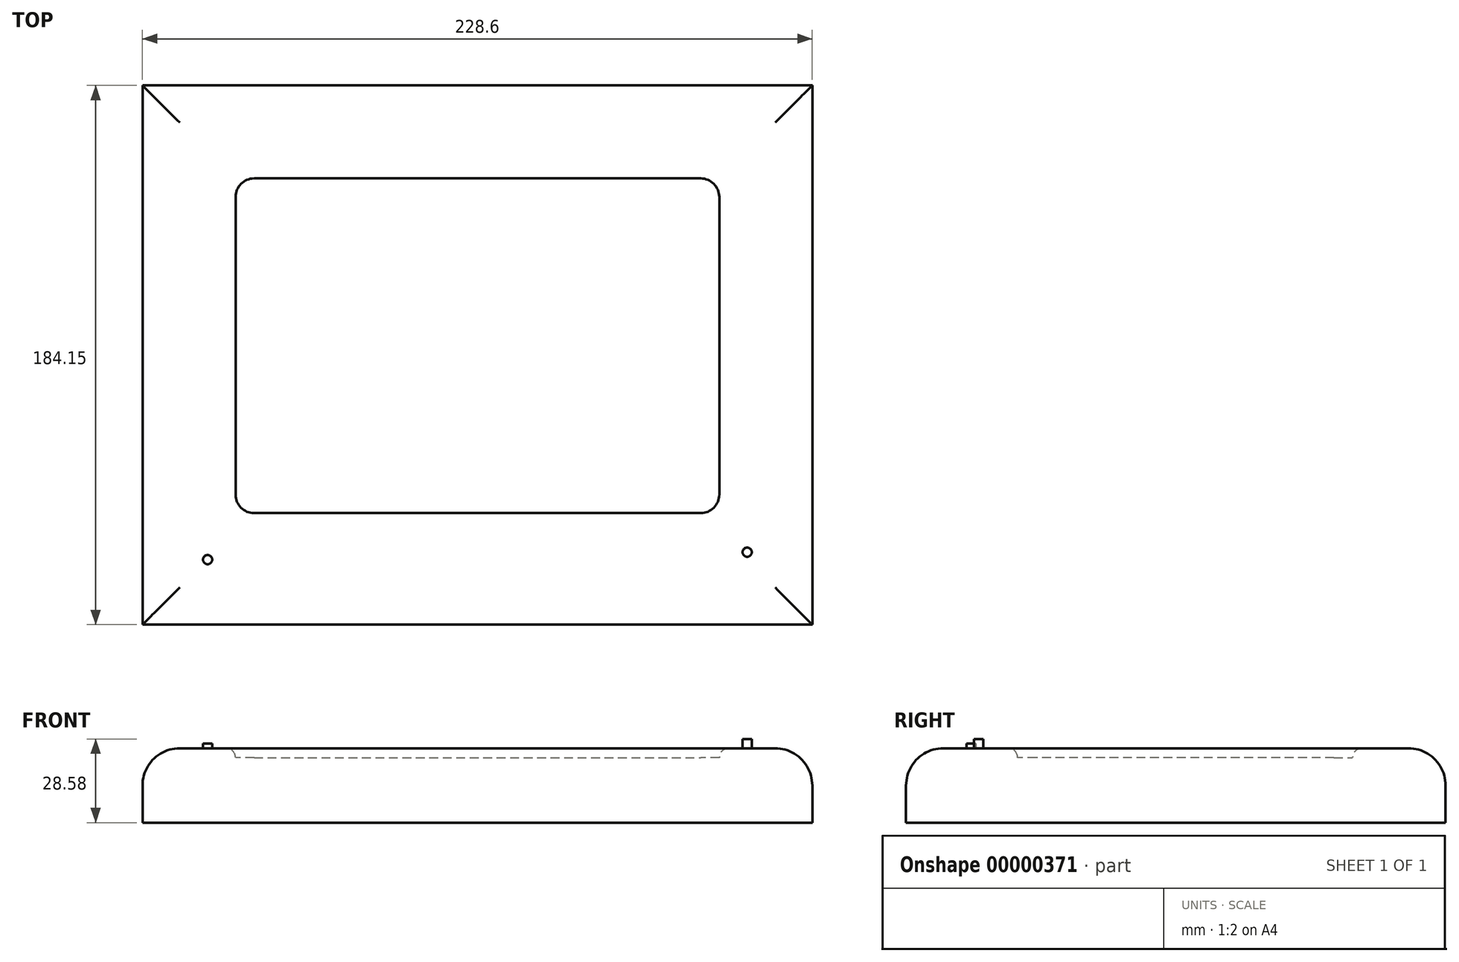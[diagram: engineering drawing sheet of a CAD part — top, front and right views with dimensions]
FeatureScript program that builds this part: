
annotation { "Feature Type Name" : "Feature", "Feature Type Description" : "" }
export const myFeature = defineFeature(function(context is Context, id is Id, definition is map)
    precondition{}
    {
        {
            var Q0;
            Q0 = qCreatedBy(makeId("Top.planeOp"), FACE);
            var sketch = newSketch(context, id + "F0", { "sketchPlane" : qUnion([Q0])});
            skLineSegment(sketch, "E0.bottom", {"start": v(-102.64, 63.45) * mm, "end": v(125.96, 63.45) * mm});
            skLineSegment(sketch, "E0.top", {"start": v(-102.64, -120.7) * mm, "end": v(125.96, -120.7) * mm});
            skLineSegment(sketch, "E0.left", {"start": v(-102.64, 63.45) * mm, "end": v(-102.64, -120.7) * mm});
            skLineSegment(sketch, "E0.right", {"start": v(125.96, 63.45) * mm, "end": v(125.96, -120.7) * mm});
            skLineSegment(sketch, "E1.bottom", {"start": v(-64.54, 31.7) * mm, "end": v(87.86, 31.7) * mm});
            skLineSegment(sketch, "E1.top", {"start": v(-64.54, -82.6) * mm, "end": v(87.86, -82.6) * mm});
            skLineSegment(sketch, "E1.left", {"start": v(-70.89, 25.35) * mm, "end": v(-70.89, -76.25) * mm});
            skLineSegment(sketch, "E1.right", {"start": v(94.21, 25.35) * mm, "end": v(94.21, -76.25) * mm});
            skPoint(sketch, "E2.visualSharp", {"position": v(-70.89, 31.7) * mm});
            skArc(sketch, "E2.filletArc", {"start": v(-64.54, 31.7) * mm, "mid": v(-69.03, 29.84) * mm, "end": v(-70.89, 25.35) * mm});
            skPoint(sketch, "E3.visualSharp", {"position": v(94.21, 31.7) * mm});
            skArc(sketch, "E3.filletArc", {"start": v(94.21, 25.35) * mm, "mid": v(92.35, 29.84) * mm, "end": v(87.86, 31.7) * mm});
            skPoint(sketch, "E4.visualSharp", {"position": v(94.21, -82.6) * mm});
            skArc(sketch, "E4.filletArc", {"start": v(87.86, -82.6) * mm, "mid": v(92.35, -80.74) * mm, "end": v(94.21, -76.25) * mm});
            skPoint(sketch, "E5.visualSharp", {"position": v(-70.89, -82.6) * mm});
            skArc(sketch, "E5.filletArc", {"start": v(-70.89, -76.25) * mm, "mid": v(-69.03, -80.74) * mm, "end": v(-64.54, -82.6) * mm});
            skSolve(sketch);
        }
        {
            var Q0;
            Q0=makeQuery(id+"F0.imprint","IMPRINT",FACE,{"disambiguationData":[TD([[makeQuery(id+"F0.imprint","IMPRINT",EDGE,{"derivedFrom":sQuery(id+"F0.wireOp",EDGE,"E1.bottom")}),-1.0]])]});
            extrude(context, id + "F1", {"entities" : qUnion([Q0]), "depth" : 22.22 * mm});
        }
        {
            var Q0;
            Q0=makeQuery(id+"F0.imprint","IMPRINT",FACE,{"disambiguationData":[TD([[makeQuery(id+"F0.imprint","IMPRINT",EDGE,{"derivedFrom":sQuery(id+"F0.wireOp",EDGE,"E0.bottom")}),-1.0]])]});
            extrude(context, id + "F2", {"entities" : qUnion([Q0]), "operationType" : NewBodyOperationType.ADD, "depth" : 25.4 * mm});
        }
        {
            var Q0;
            Q0=makeQuery(id+"F2.opExtrude","CAP_EDGE",EDGE,{"disambiguationData":[OSD([sQuery(id+"F0.wireOp",EDGE,"E0.right")])],"isStart":false});
            var Q1;
            Q1=makeQuery(id+"F2.opExtrude","CAP_EDGE",EDGE,{"disambiguationData":[OSD([sQuery(id+"F0.wireOp",EDGE,"E0.top")])],"isStart":false});
            var Q2;
            Q2=makeQuery(id+"F2.opExtrude","CAP_EDGE",EDGE,{"disambiguationData":[OSD([sQuery(id+"F0.wireOp",EDGE,"E0.left")])],"isStart":false});
            var Q3;
            Q3=makeQuery(id+"F2.opExtrude","CAP_EDGE",EDGE,{"disambiguationData":[OSD([sQuery(id+"F0.wireOp",EDGE,"E0.bottom")])],"isStart":false});
            fillet(context, id + "F3", {"entities" : qUnion([Q0, Q1, Q2, Q3]), "radius" : 12.7 * mm, "tangentPropagation" : true, "allowEdgeOverflow" : false});
        }
        {
            var Q0;
            Q0=makeQuery(id+"F2.opExtrude","CAP_EDGE",EDGE,{"disambiguationData":[OSD([sQuery(id+"F0.wireOp",EDGE,"E1.left")])],"isStart":false});
            var Q1;
            Q1=makeQuery(id+"F2.opExtrude","CAP_EDGE",EDGE,{"disambiguationData":[OSD([sQuery(id+"F0.wireOp",EDGE,"E5.filletArc")])],"isStart":false});
            var Q2;
            Q2=makeQuery(id+"F2.opExtrude","CAP_EDGE",EDGE,{"disambiguationData":[OSD([sQuery(id+"F0.wireOp",EDGE,"E1.top")])],"isStart":false});
            var Q3;
            Q3=makeQuery(id+"F2.opExtrude","CAP_EDGE",EDGE,{"disambiguationData":[OSD([sQuery(id+"F0.wireOp",EDGE,"E4.filletArc")])],"isStart":false});
            var Q4;
            Q4=makeQuery(id+"F2.opExtrude","CAP_EDGE",EDGE,{"disambiguationData":[OSD([sQuery(id+"F0.wireOp",EDGE,"E1.right")])],"isStart":false});
            var Q5;
            Q5=makeQuery(id+"F2.opExtrude","CAP_EDGE",EDGE,{"disambiguationData":[OSD([sQuery(id+"F0.wireOp",EDGE,"E3.filletArc")])],"isStart":false});
            var Q6;
            Q6=makeQuery(id+"F2.opExtrude","CAP_EDGE",EDGE,{"disambiguationData":[OSD([sQuery(id+"F0.wireOp",EDGE,"E1.bottom")])],"isStart":false});
            var Q7;
            Q7=makeQuery(id+"F2.opExtrude","CAP_EDGE",EDGE,{"disambiguationData":[OSD([sQuery(id+"F0.wireOp",EDGE,"E2.filletArc")])],"isStart":false});
            fillet(context, id + "F4", {"entities" : qUnion([Q0, Q1, Q2, Q3, Q4, Q5, Q6, Q7]), "radius" : 3.17 * mm, "tangentPropagation" : true, "allowEdgeOverflow" : false});
        }
        {
            var Q0;
            Q0=makeQuery(id+"F2.opExtrude","CAP_FACE",FACE,{"disambiguationData":[OSD([sQuery(id+"F0.wireOp",EDGE,"E0.bottom"),sQuery(id+"F0.wireOp",EDGE,"E0.top"),sQuery(id+"F0.wireOp",EDGE,"E0.left"),sQuery(id+"F0.wireOp",EDGE,"E0.right"),sQuery(id+"F0.wireOp",EDGE,"E1.bottom"),sQuery(id+"F0.wireOp",EDGE,"E1.top"),sQuery(id+"F0.wireOp",EDGE,"E1.left"),sQuery(id+"F0.wireOp",EDGE,"E1.right"),sQuery(id+"F0.wireOp",EDGE,"E2.filletArc"),sQuery(id+"F0.wireOp",EDGE,"E3.filletArc"),sQuery(id+"F0.wireOp",EDGE,"E4.filletArc"),sQuery(id+"F0.wireOp",EDGE,"E5.filletArc")])],"isStart":false});
            var sketch = newSketch(context, id + "F5", { "sketchPlane" : qUnion([Q0])});
            skCircle(sketch, "E6", {"center": v(-80.41, -98.47) * mm, "radius": 1.59 * mm});
            skCircle(sketch, "E7", {"center": v(103.74, -95.93) * mm, "radius": 1.59 * mm});
            skSolve(sketch);
        }
        {
            var Q0;
            Q0=makeQuery(id+"F5.imprint","IMPRINT",FACE,{"disambiguationData":[TD([[makeQuery(id+"F5.imprint","IMPRINT",EDGE,{"derivedFrom":sQuery(id+"F5.wireOp",EDGE,"E6")}),1.0]])]});
            extrude(context, id + "F6", {"entities" : qUnion([Q0]), "operationType" : NewBodyOperationType.ADD, "depth" : 1.59 * mm});
        }
        {
            var Q0;
            Q0=makeQuery(id+"F5.imprint","IMPRINT",FACE,{"disambiguationData":[TD([[makeQuery(id+"F5.imprint","IMPRINT",EDGE,{"derivedFrom":sQuery(id+"F5.wireOp",EDGE,"E7")}),1.0]])]});
            extrude(context, id + "F7", {"entities" : qUnion([Q0]), "operationType" : NewBodyOperationType.ADD, "depth" : 3.17 * mm});
        }
    });
